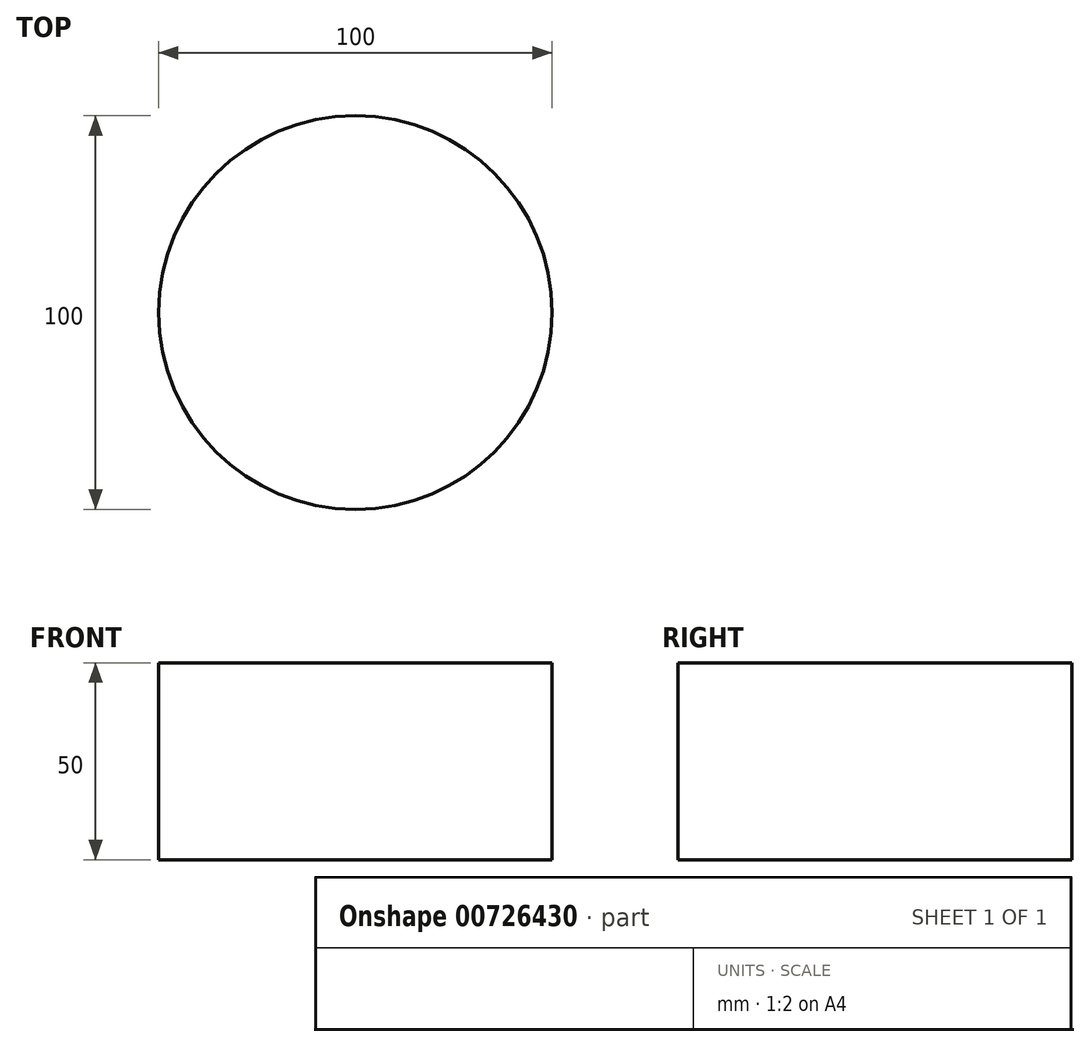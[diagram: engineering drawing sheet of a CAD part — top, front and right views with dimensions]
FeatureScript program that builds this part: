
annotation { "Feature Type Name" : "Feature", "Feature Type Description" : "" }
export const myFeature = defineFeature(function(context is Context, id is Id, definition is map)
    precondition{}
    {
        {
            var Q0;
            Q0=qCreatedBy(makeId("Top.planeOp"),FACE);
            var sketch = newSketch(context, id + "F0", { "sketchPlane" : qUnion([Q0])});
            skCircle(sketch, "E0", {"center": v(0, 0) * mm, "radius": 50 * mm});
            skSolve(sketch);
        }
        {
            var Q0;
            Q0=makeQuery(id+"F0.imprint","IMPRINT",FACE,{"disambiguationData":[TD([[makeQuery(id+"F0.imprint","IMPRINT",EDGE,{"derivedFrom":sQuery(id+"F0.wireOp",EDGE,"E0")}),1.0]])]});
            extrude(context, id + "F1", {"entities" : qUnion([Q0]), "depth" : 50 * mm, "offsetDistance" : 25 * mm});
        }
    });
